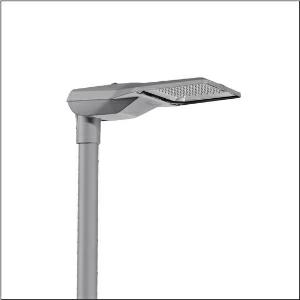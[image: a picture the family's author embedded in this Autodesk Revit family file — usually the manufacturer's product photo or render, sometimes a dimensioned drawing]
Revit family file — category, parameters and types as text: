
# Revit family: streetlight_sl_21_midi___st1_0a_5xe3d43s08mb_8ac5
name_source: partatom
category: Lighting Fixtures
units: mm (PartAtom-declared; Revit-internal decimal feet)

## family parameters
Cut with Voids When Loaded = No
Host = Face
Light Source = No
Part Type = Normal
Room Calculation Point = No
Round Connector Dimension = Use Diameter
Shared = No

## types (1)
- --- (1 x LED, 20180 lm, 147 W, 4000K)
    Apparent Load = 147 VA
    CIE Flux Codes = 37 72 97 100 100
    Color Rendering = 70
    Color Temperature = 4000K
    Default Elevation = 1800 mm
    Description = Streetlight SL 21 midi, mast luminaire, primary light control with lens, of PMMA, primary optical cover: cover, of toughened safety glass, transparent, light distribution: ST1.0a, light emission: direct distribution, primary light characteristic: asymmetric, installation type: side-entry, post-top, LED, High Power LED, rated luminous flux: 20.180lm, luminous efficacy: 137lm/W, light colour: 740, colour temperature: 4000K, control: overheat protection, constant luminous flux control, time-dependent luminous flux control, flexible luminous flux parameterisation, presetting dimming logarithmic, mains connection: 230..240V, AC, 50/60Hz, start of lifetime: 147W, end of service life: 155W, reduction: 65W, luminaire housing, of diecast aluminium, powder-coated, Siteco® metallic grey (DB 702S), corrosivity category C5 mid according to DIN EN ISO 12944, please order mast flange separately, inclination adjustable: 0°, 5°, 10°, 15°, sealing non-destructively replaceable, multi-level sealing system, length: 644mm, width: 335mm, height: 110mm, mast flange for spigot size: 42mm (side-entry): 5XC10008XM4, 60/48mm (side-entry/post-top): 5XC10108XM2, 76/60mm (side-entry/post-top): 5XC10108XM1, Smart Interface above, protection rating (complete): IP66, insulation class (complete): insulation class II (safety insulation), certification: CE, ENEC, ENEC+, VDE, impact resistance: IK09, permissible operating ambient temperature for outdoor applications: -40..+50°C, standard-compliant lighting for roads and squares, packaging unit: 1 piece

Light Distribution: ST1.0a
    Height = 111 mm
    Lamp = 1 x LED
    Lamp Light Flux = 20180 lm
    Lamp Power = 147 W
    Lamp count = 1
    Length = 644 mm
    Luminous efficacy = 137 lm/W
    Manufacturer = Siteco
    ModVariant = No
    Model = 5XE3D43S08MB
    Number of Poles = 1
    OnlyDefault = Yes
    Power Factor = 1
    Product Name = Streetlight SL 21 midi | ST1.0a
    Product group = mast luminaire | pylon top
    ProductGroupID = 6100
    Protection Class = Protection class II
    Protection Degree = IP 66
    RLX_Detail_Level = 1
    RLX_Emergency_Light_Flux = 0 lm
    RLX_Emergency_Type = 0
    RLX_Emergency_Type_DB = No
    RlxData = <blob elided: 90181 chars, md5=082021a6>
    Socket = socket
    Standby Power = 0 W
    System Light Flux = 20180 lm
    System Power = 147 W
    Type Comments = factory setting: luminous flux: 100 % | dim-lin: 254 | 750 mA
    Type Image = l_1004302.jpg
    URL = http://relux.com
    VarID = @adj_123183
    Voltage = 0 V
    Weight = 0.00 kg
    Width = 336 mm

## geometry (parser evidence)
native form markers: Blend x4, Sweep x10
no freeform markers — native parametric forms only
